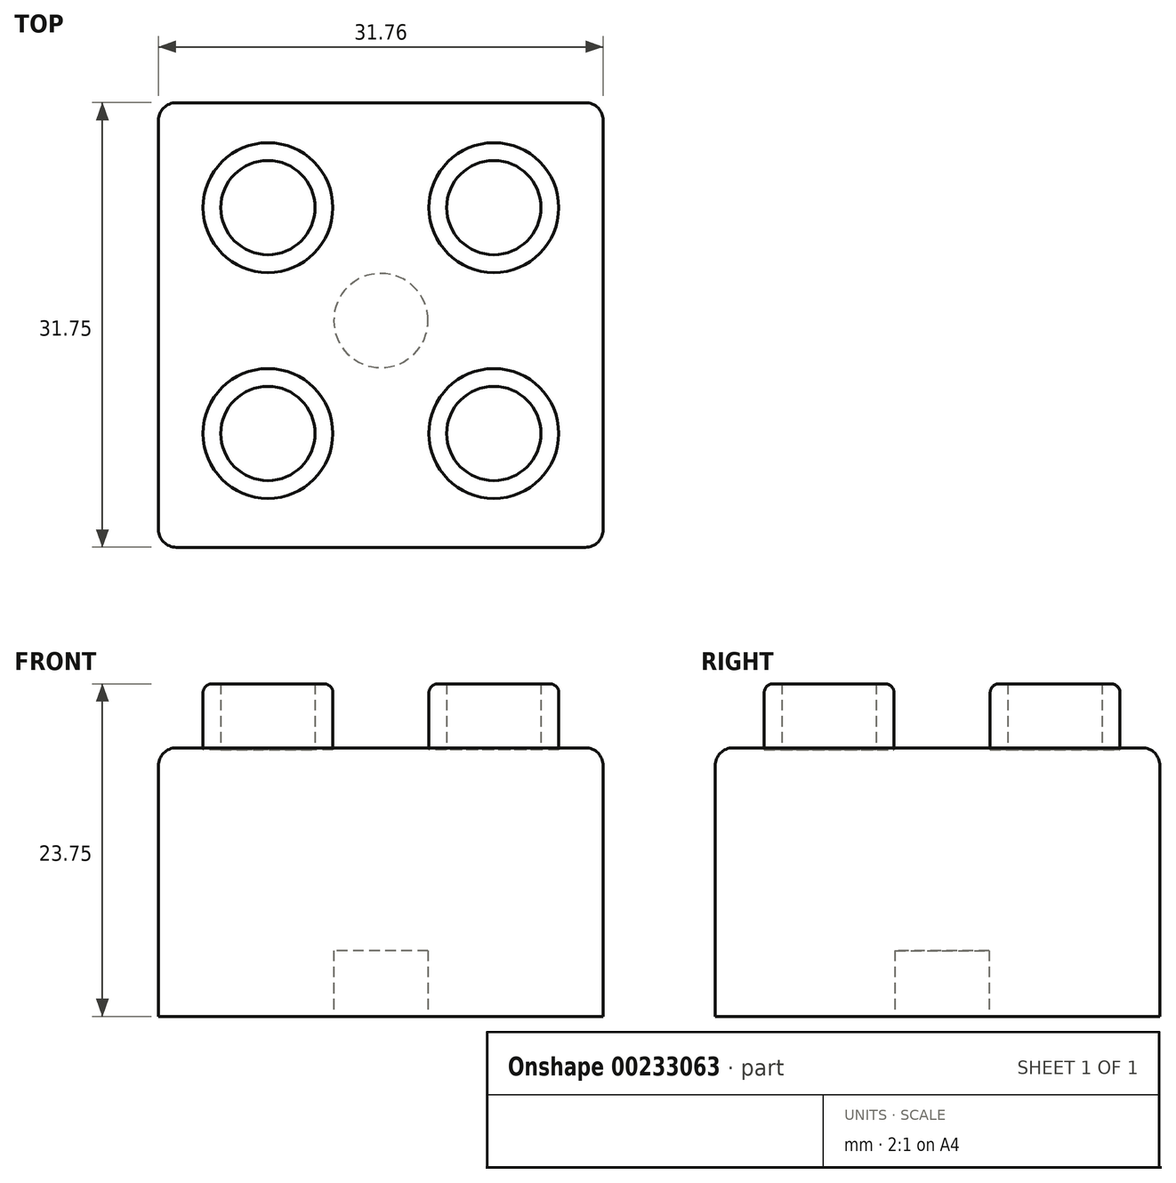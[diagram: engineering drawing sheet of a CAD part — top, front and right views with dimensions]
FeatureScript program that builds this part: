
annotation { "Feature Type Name" : "Feature", "Feature Type Description" : "" }
export const myFeature = defineFeature(function(context is Context, id is Id, definition is map)
    precondition{}
    {
        {
            var Q0;
            Q0=qCreatedBy(makeId("Top.planeOp"),FACE);
            var sketch = newSketch(context, id + "F0", { "sketchPlane" : qUnion([Q0])});
            skPoint(sketch, "E0", {"position": v(0, 16.87) * mm});
            skPoint(sketch, "E1", {"position": v(0, 15.88) * mm});
            skPoint(sketch, "E2", {"position": v(0, -14.88) * mm});
            skPoint(sketch, "E3", {"position": v(0, -15.88) * mm});
            skPoint(sketch, "E4", {"position": v(17.1, 0) * mm});
            skPoint(sketch, "E5", {"position": v(15.88, 0) * mm});
            skPoint(sketch, "E6", {"position": v(-15.88, 0) * mm});
            skPoint(sketch, "E7", {"position": v(15.64, 15.88) * mm});
            skPoint(sketch, "E8", {"position": v(15.88, 15.56) * mm});
            skPoint(sketch, "E9", {"position": v(-16.3, -15.88) * mm});
            skPoint(sketch, "E10", {"position": v(-15.88, -16.2) * mm});
            skLineSegment(sketch, "E11.bottom", {"start": v(-15.88, -16.2) * mm, "end": v(15.88, -16.2) * mm});
            skLineSegment(sketch, "E11.top", {"start": v(-15.88, 15.56) * mm, "end": v(15.88, 15.56) * mm});
            skLineSegment(sketch, "E11.left", {"start": v(-15.88, -16.2) * mm, "end": v(-15.88, 15.56) * mm});
            skLineSegment(sketch, "E11.right", {"start": v(15.88, -16.2) * mm, "end": v(15.88, 15.56) * mm});
            skSolve(sketch);
        }
        {
            var Q0;
            Q0=makeQuery(id+"F0.imprint","IMPRINT",FACE,{"disambiguationData":[TD([[makeQuery(id+"F0.imprint","IMPRINT",EDGE,{"derivedFrom":sQuery(id+"F0.wireOp",EDGE,"E11.bottom")}),1.0]])]});
            var sketch = newSketch(context, id + "F1", { "sketchPlane" : qUnion([Q0])});
            skPoint(sketch, "E12", {"position": v(14.77, 0) * mm});
            skPoint(sketch, "E13", {"position": v(14.29, 0) * mm});
            skPoint(sketch, "E14", {"position": v(-14.29, 0) * mm});
            skPoint(sketch, "E15", {"position": v(-14.29, -14.92) * mm});
            skPoint(sketch, "E16", {"position": v(-14.29, -14.29) * mm});
            skPoint(sketch, "E17", {"position": v(14.29, 14.33) * mm});
            skPoint(sketch, "E18", {"position": v(14.29, 14.29) * mm});
            skLineSegment(sketch, "E19.bottom", {"start": v(-14.29, -14.29) * mm, "end": v(14.29, -14.29) * mm});
            skLineSegment(sketch, "E19.top", {"start": v(-14.29, 14.29) * mm, "end": v(14.29, 14.29) * mm});
            skLineSegment(sketch, "E19.left", {"start": v(-14.29, -14.29) * mm, "end": v(-14.29, 14.29) * mm});
            skLineSegment(sketch, "E19.right", {"start": v(14.29, -14.29) * mm, "end": v(14.29, 14.29) * mm});
            skSolve(sketch);
        }
        {
            var Q0;
            Q0=makeQuery(id+"F1.imprint","IMPRINT",FACE,{"disambiguationData":[TD([[makeQuery(id+"F1.imprint","IMPRINT",EDGE,{"derivedFrom":sQuery(id+"F1.wireOp",EDGE,"E19.bottom")}),1.0]])]});
            var sketch = newSketch(context, id + "F2", { "sketchPlane" : qUnion([Q0])});
            skPoint(sketch, "E20", {"position": v(0, 0) * mm});
            skCircle(sketch, "E21", {"center": v(0, 0) * mm, "radius": 6.54 * mm});
            skSolve(sketch);
        }
        {
            var Q0;
            Q0=qSketchRegion(id+"F0",true);
            extrude(context, id + "F3", {"entities" : qUnion([Q0]), "depth" : 19.18 * mm});
        }
        {
            var Q0;
            Q0=qSketchRegion(id+"F2",true);
            extrude(context, id + "F4", {"entities" : qUnion([Q0]), "operationType" : NewBodyOperationType.ADD, "depth" : 15.88 * mm});
        }
        {
            var Q0;
            Q0=qCreatedBy(makeId("Top.planeOp"),FACE);
            var sketch = newSketch(context, id + "F5", { "sketchPlane" : qUnion([Q0])});
            skCircle(sketch, "E22", {"center": v(0, 0) * mm, "radius": 4.64 * mm});
            skSolve(sketch);
        }
        {
            var Q0;
            Q0=qCreatedBy(makeId("Top.planeOp"),FACE);
            var sketch = newSketch(context, id + "F6", { "sketchPlane" : qUnion([Q0])});
            skCircle(sketch, "E23", {"center": v(0, 0) * mm, "radius": 3.37 * mm});
            skSolve(sketch);
        }
        {
            var Q0;
            Q0=makeQuery(id+"F5.imprint","IMPRINT",FACE,{"disambiguationData":[TD([[makeQuery(id+"F5.imprint","IMPRINT",EDGE,{"derivedFrom":sQuery(id+"F5.wireOp",EDGE,"E22")}),1.0]])]});
            extrude(context, id + "F7", {"entities" : qUnion([Q0]), "depth" : 4.7 * mm});
        }
        {
            var Q0;
            Q0=makeQuery(id+"F6.imprint","IMPRINT",FACE,{"disambiguationData":[TD([[makeQuery(id+"F6.imprint","IMPRINT",EDGE,{"derivedFrom":sQuery(id+"F6.wireOp",EDGE,"E23")}),1.0]])]});
            extrude(context, id + "F8", {"entities" : qUnion([Q0]), "operationType" : NewBodyOperationType.REMOVE, "depth" : 4.7 * mm});
        }
        {
            var Q0;
            Q0=makeQuery(id+"F7.opExtrude","SWEPT_BODY",BODY,{"disambiguationData":[OSD([sQuery(id+"F5.wireOp",EDGE,"E22")])]});
            transform(context, id + "F9", {"entities" : qUnion([Q0]), "transformType" : TransformType.TRANSLATION_3D, "dx" : 8.06 * mm, "dy" : 8.06 * mm, "dz" : 19.05 * mm, "makeCopy" : false});
        }
        {
            var Q0;
            Q0=makeQuery(id+"F7.opExtrude","SWEPT_BODY",BODY,{"disambiguationData":[OSD([sQuery(id+"F5.wireOp",EDGE,"E22")])]});
            var Q1;
            Q1=qCreatedBy(makeId("Front.planeOp"),FACE);
            mirror(context, id + "F10", {"entities" : qUnion([Q0]), "mirrorPlane" : qUnion([Q1])});
        }
        {
            var Q0;
            Q0=makeQuery(id+"F7.opExtrude","SWEPT_BODY",BODY,{"disambiguationData":[OSD([sQuery(id+"F5.wireOp",EDGE,"E22")])]});
            var Q1;
            Q1=makeQuery(id+"F10.opPattern","COPY",BODY,{"derivedFrom":makeQuery(id+"F7.opExtrude","SWEPT_BODY",BODY,{"disambiguationData":[OSD([sQuery(id+"F5.wireOp",EDGE,"E22")])]}),"instanceName":"1"});
            var Q2;
            Q2=qCreatedBy(makeId("Right.planeOp"),FACE);
            mirror(context, id + "F11", {"entities" : qUnion([Q0, Q1]), "mirrorPlane" : qUnion([Q2])});
        }
        {
            var Q0;
            Q0=makeQuery(id+"F3.opExtrude","CAP_EDGE",EDGE,{"disambiguationData":[OSD([sQuery(id+"F0.wireOp",EDGE,"E11.bottom")])],"isStart":false});
            var Q1;
            Q1=makeQuery(id+"F3.opExtrude","CAP_EDGE",EDGE,{"disambiguationData":[OSD([sQuery(id+"F0.wireOp",EDGE,"E11.left")])],"isStart":false});
            var Q2;
            Q2=makeQuery(id+"F3.opExtrude","CAP_EDGE",EDGE,{"disambiguationData":[OSD([sQuery(id+"F0.wireOp",EDGE,"E11.top")])],"isStart":false});
            var Q3;
            Q3=makeQuery(id+"F3.opExtrude","CAP_EDGE",EDGE,{"disambiguationData":[OSD([sQuery(id+"F0.wireOp",EDGE,"E11.right")])],"isStart":false});
            var Q4;
            Q4=makeQuery(id+"F3.opExtrude","SWEPT_EDGE",EDGE,{"disambiguationData":[OSD([sQuery(id+"F0.wireOp",EDGE,"E11.bottom"),sQuery(id+"F0.wireOp",EDGE,"E11.left")])]});
            var Q5;
            Q5=makeQuery(id+"F3.opExtrude","SWEPT_EDGE",EDGE,{"disambiguationData":[OSD([sQuery(id+"F0.wireOp",EDGE,"E11.bottom"),sQuery(id+"F0.wireOp",EDGE,"E11.right")])]});
            var Q6;
            Q6=makeQuery(id+"F3.opExtrude","SWEPT_EDGE",EDGE,{"disambiguationData":[OSD([sQuery(id+"F0.wireOp",EDGE,"E11.top"),sQuery(id+"F0.wireOp",EDGE,"E11.left")])]});
            var Q7;
            Q7=makeQuery(id+"F3.opExtrude","SWEPT_EDGE",EDGE,{"disambiguationData":[OSD([sQuery(id+"F0.wireOp",EDGE,"E11.top"),sQuery(id+"F0.wireOp",EDGE,"E11.right")])]});
            fillet(context, id + "F12", {"entities" : qUnion([Q0, Q1, Q2, Q3, Q4, Q5, Q6, Q7]), "radius" : 1.27 * mm, "tangentPropagation" : true, "allowEdgeOverflow" : false});
        }
        {
            var Q0;
            Q0=makeQuery(id+"F11.opPattern","COPY",EDGE,{"derivedFrom":makeQuery(id+"F7.opExtrude","CAP_EDGE",EDGE,{"disambiguationData":[OSD([sQuery(id+"F5.wireOp",EDGE,"E22")])],"isStart":false}),"instanceName":"1"});
            var Q1;
            Q1=makeQuery(id+"F7.opExtrude","CAP_EDGE",EDGE,{"disambiguationData":[OSD([sQuery(id+"F5.wireOp",EDGE,"E22")])],"isStart":false});
            var Q2;
            Q2=makeQuery(id+"F10.opPattern","COPY",EDGE,{"derivedFrom":makeQuery(id+"F7.opExtrude","CAP_EDGE",EDGE,{"disambiguationData":[OSD([sQuery(id+"F5.wireOp",EDGE,"E22")])],"isStart":false}),"instanceName":"1"});
            var Q3;
            Q3=makeQuery(id+"F11.opPattern","COPY",EDGE,{"derivedFrom":makeQuery(id+"F10.opPattern","COPY",EDGE,{"derivedFrom":makeQuery(id+"F7.opExtrude","CAP_EDGE",EDGE,{"disambiguationData":[OSD([sQuery(id+"F5.wireOp",EDGE,"E22")])],"isStart":false}),"instanceName":"1"}),"instanceName":"1"});
            fillet(context, id + "F13", {"entities" : qUnion([Q0, Q1, Q2, Q3]), "radius" : 0.64 * mm, "tangentPropagation" : true, "allowEdgeOverflow" : false});
        }
    });
